# Revit family: 265-91-001 DN0900-1000
name_source: partatom
category: Pipe Accessories
units: mm (PartAtom-declared; Revit-internal decimal feet)

## family parameters
Always vertical = Yes
Cut with Voids When Loaded = No
Part Type = Valve - Breaks Into
Round Connector Dimension = Use Diameter
Shared = No
Work Plane-Based = No

## types (4) — shared parameters
25 = 25 mm  [stored 0.082021 ft]
Bolt.no = 28 mm  [stored 0.0918635 ft]
DN0900_PN10 = 265-9-0900-11-04036401
DN0900_PN16 = 265-9-0900-10-14036400
DN1000_PN10 = 265-9-1000-11-04036401
DN1000_PN16 = 265-9-1000-10-14036400
Description_ = AVK DISMANTLING JOINT WITH CENTRE FLANGE, PN10/16
Raised_dis = 5 mm  [stored 0.0164042 ft]
Search_table = 265-91-001 DN0900-1000
URL_product_pages = https://www.avkvalves.com
zero-valued in all types: Default Elevation

## per-type parameters (varying)
| type | B1 | Bore | D | DN | FL_T | FL_T/2 | L | L1 | L11 | L2 | L3 | Nut_T | PCD | PN | S | S11 | T | T1 | offset | raised_R |
| DN0900_PN16 | 44 mm | 450 mm | 563 mm | 900 mm | 47 mm | 23 mm | 545 mm | 218 mm | 320 mm  [stored 1.04987 ft] | 35 mm  [stored 0.114829 ft] | 23 mm | 19 mm  [stored 0.062336 ft] | 525 mm | 16 mm  [stored 0.0524934 ft] | 36 mm  [stored 0.11811 ft] | 49 mm | 14 mm  [stored 0.0459318 ft] | 35 mm  [stored 0.114829 ft] | 13 mm  [stored 0.0426509 ft] | 478 mm |
| DN0900_PN10 | 38 mm | 450 mm | 558 mm | 900 mm | 40 mm  [stored 0.131234 ft] | 20 mm  [stored 0.0656168 ft] | 480 mm | 197 mm | 290 mm  [stored 0.951444 ft] | 31 mm | 20 mm  [stored 0.0656168 ft] | 16 mm  [stored 0.0524934 ft] | 525 mm | 10 mm  [stored 0.0328084 ft] | 30 mm  [stored 0.0984252 ft] | 41 mm | 12 mm  [stored 0.0393701 ft] | 30 mm  [stored 0.0984252 ft] | 11 mm | 474 mm |
| DN1000_PN16 | 46 mm | 500 mm | 628 mm | 1000 mm | 50 mm  [stored 0.164042 ft] | 25 mm  [stored 0.082021 ft] | 580 mm | 231 mm | 340 mm  [stored 1.11549 ft] | 38 mm | 25 mm  [stored 0.082021 ft] | 20 mm  [stored 0.0656168 ft] | 585 mm | 16 mm  [stored 0.0524934 ft] | 39 mm  [stored 0.127953 ft] | 53 mm | 15 mm  [stored 0.0492126 ft] | 38 mm | 14 mm  [stored 0.0459318 ft] | 533 mm |
| DN1000_PN10 | 40 mm  [stored 0.131234 ft] | 500 mm | 615 mm | 1000 mm | 43 mm  [stored 0.141076 ft] | 21 mm | 500 mm | 197 mm | 290 mm  [stored 0.951444 ft] | 33 mm  [stored 0.108268 ft] | 21 mm | 17 mm | 580 mm | 10 mm  [stored 0.0328084 ft] | 33 mm  [stored 0.108268 ft] | 45 mm  [stored 0.147638 ft] | 13 mm  [stored 0.0426509 ft] | 32 mm  [stored 0.104987 ft] | 12 mm  [stored 0.0393701 ft] | 523 mm |

note: [stored X ft] marks values corroborated as IEEE doubles in the binary element streams (Revit-internal decimal feet)

## geometry (parser evidence)
native form markers: Sweep x7
no freeform markers — native parametric forms only
